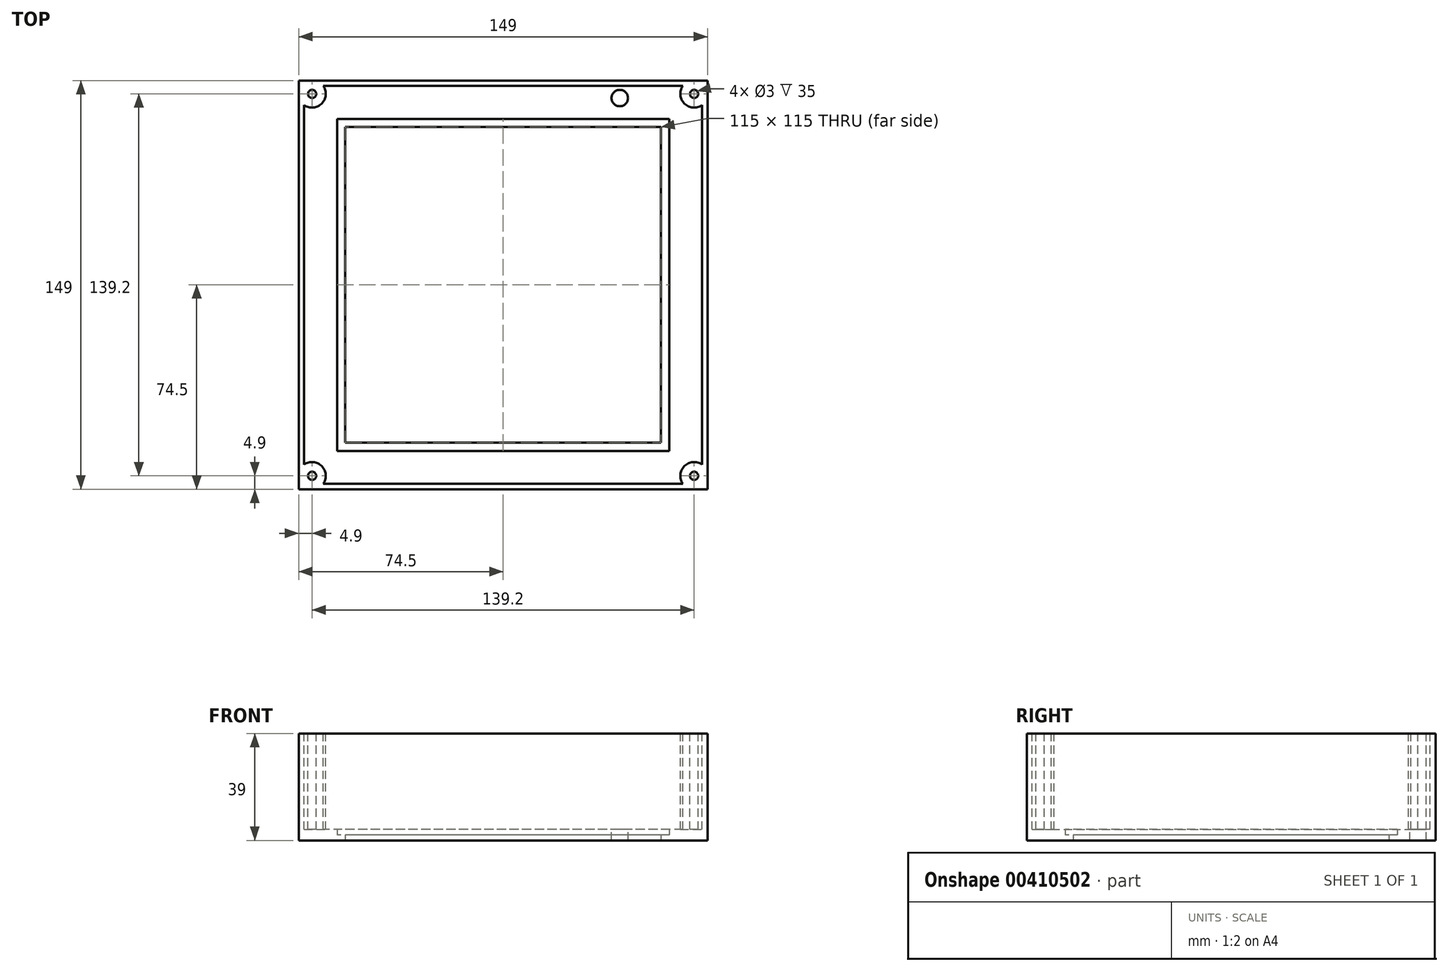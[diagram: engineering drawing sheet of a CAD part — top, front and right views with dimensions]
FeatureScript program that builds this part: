
annotation { "Feature Type Name" : "Feature", "Feature Type Description" : "" }
export const myFeature = defineFeature(function(context is Context, id is Id, definition is map)
    precondition{}
    {
        {
            var Q0;
            Q0=qCreatedBy(makeId("Top.planeOp"),FACE);
            var sketch = newSketch(context, id + "F0", { "sketchPlane" : qUnion([Q0])});
            skLineSegment(sketch, "E0.bottom", {"start": v(60.5, 60.5) * mm, "end": v(-60.5, 60.5) * mm});
            skLineSegment(sketch, "E0.top", {"start": v(60.5, -60.5) * mm, "end": v(-60.5, -60.5) * mm});
            skLineSegment(sketch, "E0.left", {"start": v(60.5, 60.5) * mm, "end": v(60.5, -60.5) * mm});
            skLineSegment(sketch, "E0.right", {"start": v(-60.5, 60.5) * mm, "end": v(-60.5, -60.5) * mm});
            skLineSegment(sketch, "E1.0", {"start": v(60.5, 57.5) * mm, "end": v(-60.5, 57.5) * mm});
            skLineSegment(sketch, "E2.0", {"start": v(57.5, 60.5) * mm, "end": v(57.5, -60.5) * mm});
            skLineSegment(sketch, "E3.0", {"start": v(60.5, -57.5) * mm, "end": v(-60.5, -57.5) * mm});
            skLineSegment(sketch, "E4.0", {"start": v(-57.5, 60.5) * mm, "end": v(-57.5, -60.5) * mm});
            skLineSegment(sketch, "E5.0", {"start": v(60.5, 74.5) * mm, "end": v(-60.5, 74.5) * mm});
            skLineSegment(sketch, "E6.0", {"start": v(60.5, -74.5) * mm, "end": v(-60.5, -74.5) * mm});
            skLineSegment(sketch, "E7.0", {"start": v(-74.5, 60.5) * mm, "end": v(-74.5, -60.5) * mm});
            skLineSegment(sketch, "E8.0", {"start": v(74.5, 60.5) * mm, "end": v(74.5, -60.5) * mm});
            skLineSegment(sketch, "E9", {"start": v(-74.5, 60.5) * mm, "end": v(-74.5, 74.5) * mm});
            skLineSegment(sketch, "E10", {"start": v(-60.5, 74.5) * mm, "end": v(-74.5, 74.5) * mm});
            skLineSegment(sketch, "E11", {"start": v(60.5, 74.5) * mm, "end": v(74.5, 74.5) * mm});
            skLineSegment(sketch, "E12", {"start": v(74.5, 60.5) * mm, "end": v(74.5, 74.5) * mm});
            skLineSegment(sketch, "E13", {"start": v(74.5, -60.5) * mm, "end": v(74.5, -74.5) * mm});
            skLineSegment(sketch, "E14", {"start": v(60.5, -74.5) * mm, "end": v(74.5, -74.5) * mm});
            skLineSegment(sketch, "E15", {"start": v(-60.5, -74.5) * mm, "end": v(-74.5, -74.5) * mm});
            skLineSegment(sketch, "E16", {"start": v(-74.5, -60.5) * mm, "end": v(-74.5, -74.5) * mm});
            skPoint(sketch, "E17.orphan", {"position": v(82.8, 74.5) * mm});
            skSolve(sketch);
        }
        {
            var Q0;
            Q0=makeQuery(id+"F0.imprint","IMPRINT",FACE,{"disambiguationData":[TD([[makeQuery(id+"F0.imprint","IMPRINT",EDGE,{"derivedFrom":sQuery(id+"F0.wireOp",EDGE,"E5.0")}),1.0]])]});
            extrude(context, id + "F1", {"entities" : qUnion([Q0]), "depth" : 4 * mm});
        }
        {
            var Q0;
            {var subQ0=sQuery(id+"F0.wireOp",EDGE,"E2.0");var subQ1=sQuery(id+"F0.wireOp",EDGE,"E0.bottom");var subQ2=makeQuery(id+"F0.imprint","INTERSECT",VERTEX,{"derivedFrom":[subQ1,subQ0]});Q0=makeQuery(id+"F0.imprint","IMPRINT",FACE,{"disambiguationData":[TD([[makeQuery(id+"F0.imprint","IMPRINT",EDGE,{"disambiguationData":[TD([[subQ2,-1.0]])],"derivedFrom":subQ1}),1.0]])]});}
            var Q1;
            {var subQ0=sQuery(id+"F0.wireOp",EDGE,"E0.left");var subQ1=sQuery(id+"F0.wireOp",EDGE,"E0.bottom");var subQ2=makeQuery(id+"F0.imprint","INTERSECT",VERTEX,{"derivedFrom":[subQ1,subQ0]});Q1=makeQuery(id+"F0.imprint","IMPRINT",FACE,{"disambiguationData":[TD([[makeQuery(id+"F0.imprint","IMPRINT",EDGE,{"disambiguationData":[TD([[subQ2,-1.0]])],"derivedFrom":subQ1}),1.0]])]});}
            var Q2;
            {var subQ0=sQuery(id+"F0.wireOp",EDGE,"E1.0");var subQ1=sQuery(id+"F0.wireOp",EDGE,"E0.left");var subQ2=makeQuery(id+"F0.imprint","INTERSECT",VERTEX,{"derivedFrom":[subQ1,subQ0]});Q2=makeQuery(id+"F0.imprint","IMPRINT",FACE,{"disambiguationData":[TD([[makeQuery(id+"F0.imprint","IMPRINT",EDGE,{"disambiguationData":[TD([[subQ2,-1.0]])],"derivedFrom":subQ1}),-1.0]])]});}
            var Q3;
            {var subQ0=sQuery(id+"F0.wireOp",EDGE,"E0.left");var subQ1=sQuery(id+"F0.wireOp",EDGE,"E0.top");var subQ2=makeQuery(id+"F0.imprint","INTERSECT",VERTEX,{"derivedFrom":[subQ1,subQ0]});Q3=makeQuery(id+"F0.imprint","IMPRINT",FACE,{"disambiguationData":[TD([[makeQuery(id+"F0.imprint","IMPRINT",EDGE,{"disambiguationData":[TD([[subQ2,-1.0]])],"derivedFrom":subQ1}),-1.0]])]});}
            var Q4;
            {var subQ0=sQuery(id+"F0.wireOp",EDGE,"E2.0");var subQ1=sQuery(id+"F0.wireOp",EDGE,"E0.top");var subQ2=makeQuery(id+"F0.imprint","INTERSECT",VERTEX,{"derivedFrom":[subQ1,subQ0]});Q4=makeQuery(id+"F0.imprint","IMPRINT",FACE,{"disambiguationData":[TD([[makeQuery(id+"F0.imprint","IMPRINT",EDGE,{"disambiguationData":[TD([[subQ2,-1.0]])],"derivedFrom":subQ1}),-1.0]])]});}
            var Q5;
            {var subQ0=sQuery(id+"F0.wireOp",EDGE,"E1.0");var subQ1=sQuery(id+"F0.wireOp",EDGE,"E0.right");var subQ2=makeQuery(id+"F0.imprint","INTERSECT",VERTEX,{"derivedFrom":[subQ1,subQ0]});Q5=makeQuery(id+"F0.imprint","IMPRINT",FACE,{"disambiguationData":[TD([[makeQuery(id+"F0.imprint","IMPRINT",EDGE,{"disambiguationData":[TD([[subQ2,-1.0]])],"derivedFrom":subQ1}),1.0]])]});}
            var Q6;
            {var subQ0=sQuery(id+"F0.wireOp",EDGE,"E0.right");var subQ1=sQuery(id+"F0.wireOp",EDGE,"E0.top");var subQ2=makeQuery(id+"F0.imprint","INTERSECT",VERTEX,{"derivedFrom":[subQ1,subQ0]});Q6=makeQuery(id+"F0.imprint","IMPRINT",FACE,{"disambiguationData":[TD([[makeQuery(id+"F0.imprint","IMPRINT",EDGE,{"disambiguationData":[TD([[subQ2,1.0]])],"derivedFrom":subQ1}),-1.0]])]});}
            var Q7;
            {var subQ0=sQuery(id+"F0.wireOp",EDGE,"E0.right");var subQ1=sQuery(id+"F0.wireOp",EDGE,"E0.bottom");var subQ2=makeQuery(id+"F0.imprint","INTERSECT",VERTEX,{"derivedFrom":[subQ1,subQ0]});Q7=makeQuery(id+"F0.imprint","IMPRINT",FACE,{"disambiguationData":[TD([[makeQuery(id+"F0.imprint","IMPRINT",EDGE,{"disambiguationData":[TD([[subQ2,1.0]])],"derivedFrom":subQ1}),1.0]])]});}
            extrude(context, id + "F2", {"entities" : qUnion([Q0, Q1, Q2, Q3, Q4, Q5, Q6, Q7]), "operationType" : NewBodyOperationType.ADD, "depth" : 2 * mm});
        }
        {
            var Q0;
            Q0=makeQuery(id+"F1.opExtrude","CAP_FACE",FACE,{"disambiguationData":[OSD([sQuery(id+"F0.wireOp",EDGE,"E0.bottom"),sQuery(id+"F0.wireOp",EDGE,"E0.top"),sQuery(id+"F0.wireOp",EDGE,"E0.left"),sQuery(id+"F0.wireOp",EDGE,"E0.right"),sQuery(id+"F0.wireOp",EDGE,"E5.0"),sQuery(id+"F0.wireOp",EDGE,"E6.0"),sQuery(id+"F0.wireOp",EDGE,"E7.0"),sQuery(id+"F0.wireOp",EDGE,"E8.0"),sQuery(id+"F0.wireOp",EDGE,"E9"),sQuery(id+"F0.wireOp",EDGE,"E10"),sQuery(id+"F0.wireOp",EDGE,"E11"),sQuery(id+"F0.wireOp",EDGE,"E12"),sQuery(id+"F0.wireOp",EDGE,"E13"),sQuery(id+"F0.wireOp",EDGE,"E14"),sQuery(id+"F0.wireOp",EDGE,"E15"),sQuery(id+"F0.wireOp",EDGE,"E16")])],"isStart":false});
            var sketch = newSketch(context, id + "F3", { "sketchPlane" : qUnion([Q0])});
            skCircle(sketch, "E18", {"center": v(42.52, 68.09) * mm, "radius": 3 * mm});
            skSolve(sketch);
        }
        {
            var Q0;
            Q0=makeQuery(id+"F3.imprint","IMPRINT",FACE,{"disambiguationData":[TD([[makeQuery(id+"F3.imprint","IMPRINT",EDGE,{"derivedFrom":sQuery(id+"F3.wireOp",EDGE,"E18")}),1.0]])]});
            extrude(context, id + "F4", {"entities" : qUnion([Q0]), "operationType" : NewBodyOperationType.REMOVE, "endBound" : BoundingType.UP_TO_NEXT, "oppositeDirection" : true, "depth" : 25 * mm});
        }
        {
            var Q0;
            Q0=makeQuery(id+"F1.opExtrude","CAP_FACE",FACE,{"disambiguationData":[OSD([sQuery(id+"F0.wireOp",EDGE,"E0.bottom"),sQuery(id+"F0.wireOp",EDGE,"E0.top"),sQuery(id+"F0.wireOp",EDGE,"E0.left"),sQuery(id+"F0.wireOp",EDGE,"E0.right"),sQuery(id+"F0.wireOp",EDGE,"E5.0"),sQuery(id+"F0.wireOp",EDGE,"E6.0"),sQuery(id+"F0.wireOp",EDGE,"E7.0"),sQuery(id+"F0.wireOp",EDGE,"E8.0"),sQuery(id+"F0.wireOp",EDGE,"E9"),sQuery(id+"F0.wireOp",EDGE,"E10"),sQuery(id+"F0.wireOp",EDGE,"E11"),sQuery(id+"F0.wireOp",EDGE,"E12"),sQuery(id+"F0.wireOp",EDGE,"E13"),sQuery(id+"F0.wireOp",EDGE,"E14"),sQuery(id+"F0.wireOp",EDGE,"E15"),sQuery(id+"F0.wireOp",EDGE,"E16")])],"isStart":false});
            var sketch = newSketch(context, id + "F5", { "sketchPlane" : qUnion([Q0])});
            skLineSegment(sketch, "E19.0", {"start": v(60.5, 72.5) * mm, "end": v(72.5, 72.5) * mm});
            skLineSegment(sketch, "E19.1", {"start": v(-72.5, -60.5) * mm, "end": v(-72.5, -72.5) * mm});
            skLineSegment(sketch, "E19.2", {"start": v(-72.5, 60.5) * mm, "end": v(-72.5, -60.5) * mm});
            skLineSegment(sketch, "E19.3", {"start": v(-72.5, 60.5) * mm, "end": v(-72.5, 72.5) * mm});
            skLineSegment(sketch, "E19.4", {"start": v(-60.5, 72.5) * mm, "end": v(-72.5, 72.5) * mm});
            skLineSegment(sketch, "E19.5", {"start": v(-60.5, -72.5) * mm, "end": v(-72.5, -72.5) * mm});
            skLineSegment(sketch, "E19.6", {"start": v(60.5, 72.5) * mm, "end": v(-60.5, 72.5) * mm});
            skLineSegment(sketch, "E19.7", {"start": v(60.5, -72.5) * mm, "end": v(-60.5, -72.5) * mm});
            skLineSegment(sketch, "E19.8", {"start": v(60.5, -72.5) * mm, "end": v(72.5, -72.5) * mm});
            skLineSegment(sketch, "E19.9", {"start": v(72.5, -60.5) * mm, "end": v(72.5, -72.5) * mm});
            skLineSegment(sketch, "E19.10", {"start": v(72.5, 60.5) * mm, "end": v(72.5, -60.5) * mm});
            skLineSegment(sketch, "E19.11", {"start": v(72.5, 60.5) * mm, "end": v(72.5, 72.5) * mm});
            skSolve(sketch);
        }
        {
            var Q0;
            Q0=makeQuery(id+"F5.imprint","IMPRINT",FACE,{"disambiguationData":[TD([[makeQuery(id+"F5.imprint","IMPRINT",EDGE,{"derivedFrom":sQuery(id+"F5.wireOp",EDGE,"E19.0")}),1.0]])]});
            extrude(context, id + "F6", {"entities" : qUnion([Q0]), "operationType" : NewBodyOperationType.ADD, "depth" : 35 * mm});
        }
        {
            var Q0;
            Q0=makeQuery(id+"F6.opExtrude","CAP_FACE",FACE,{"disambiguationData":[OSD([sQuery(id+"F0.wireOp",EDGE,"E5.0"),sQuery(id+"F0.wireOp",EDGE,"E6.0"),sQuery(id+"F0.wireOp",EDGE,"E7.0"),sQuery(id+"F0.wireOp",EDGE,"E8.0"),sQuery(id+"F0.wireOp",EDGE,"E9"),sQuery(id+"F0.wireOp",EDGE,"E10"),sQuery(id+"F0.wireOp",EDGE,"E11"),sQuery(id+"F0.wireOp",EDGE,"E12"),sQuery(id+"F0.wireOp",EDGE,"E13"),sQuery(id+"F0.wireOp",EDGE,"E14"),sQuery(id+"F0.wireOp",EDGE,"E15"),sQuery(id+"F0.wireOp",EDGE,"E16"),sQuery(id+"F5.wireOp",EDGE,"E19.0"),sQuery(id+"F5.wireOp",EDGE,"E19.1"),sQuery(id+"F5.wireOp",EDGE,"E19.2"),sQuery(id+"F5.wireOp",EDGE,"E19.3"),sQuery(id+"F5.wireOp",EDGE,"E19.4"),sQuery(id+"F5.wireOp",EDGE,"E19.5"),sQuery(id+"F5.wireOp",EDGE,"E19.6"),sQuery(id+"F5.wireOp",EDGE,"E19.7"),sQuery(id+"F5.wireOp",EDGE,"E19.8"),sQuery(id+"F5.wireOp",EDGE,"E19.9"),sQuery(id+"F5.wireOp",EDGE,"E19.10"),sQuery(id+"F5.wireOp",EDGE,"E19.11")])],"isStart":false});
            var sketch = newSketch(context, id + "F7", { "sketchPlane" : qUnion([Q0])});
            skCircle(sketch, "E20", {"center": v(-69.6, 69.6) * mm, "radius": 5 * mm});
            skCircle(sketch, "E21", {"center": v(-69.6, 69.6) * mm, "radius": 1.5 * mm});
            skCircle(sketch, "E22.1.0", {"center": v(-69.6, -69.6) * mm, "radius": 5 * mm});
            skCircle(sketch, "E22.1.1", {"center": v(-69.6, -69.6) * mm, "radius": 1.5 * mm});
            skCircle(sketch, "E22.2.0", {"center": v(69.6, -69.6) * mm, "radius": 5 * mm});
            skCircle(sketch, "E22.2.1", {"center": v(69.6, -69.6) * mm, "radius": 1.5 * mm});
            skCircle(sketch, "E22.3.0", {"center": v(69.6, 69.6) * mm, "radius": 5 * mm});
            skCircle(sketch, "E22.3.1", {"center": v(69.6, 69.6) * mm, "radius": 1.5 * mm});
            skPoint(sketch, "E22.center", {"position": v(0, 0) * mm});
            skSolve(sketch);
        }
        {
            var Q0;
            Q0=makeQuery(id+"F7.imprint","IMPRINT",FACE,{"disambiguationData":[TD([[makeQuery(id+"F7.imprint","IMPRINT",EDGE,{"derivedFrom":sQuery(id+"F7.wireOp",EDGE,"E21")}),-1.0]])]});
            var Q1;
            Q1=makeQuery(id+"F7.imprint","IMPRINT",FACE,{"disambiguationData":[TD([[makeQuery(id+"F7.imprint","IMPRINT",EDGE,{"derivedFrom":sQuery(id+"F7.wireOp",EDGE,"E22.3.1")}),-1.0]])]});
            var Q2;
            Q2=makeQuery(id+"F7.imprint","IMPRINT",FACE,{"disambiguationData":[TD([[makeQuery(id+"F7.imprint","IMPRINT",EDGE,{"derivedFrom":sQuery(id+"F7.wireOp",EDGE,"E22.2.1")}),-1.0]])]});
            var Q3;
            Q3=makeQuery(id+"F7.imprint","IMPRINT",FACE,{"disambiguationData":[TD([[makeQuery(id+"F7.imprint","IMPRINT",EDGE,{"derivedFrom":sQuery(id+"F7.wireOp",EDGE,"E22.1.1")}),-1.0]])]});
            extrude(context, id + "F8", {"entities" : qUnion([Q0, Q1, Q2, Q3]), "operationType" : NewBodyOperationType.ADD, "oppositeDirection" : true, "depth" : 35 * mm});
        }
    });
